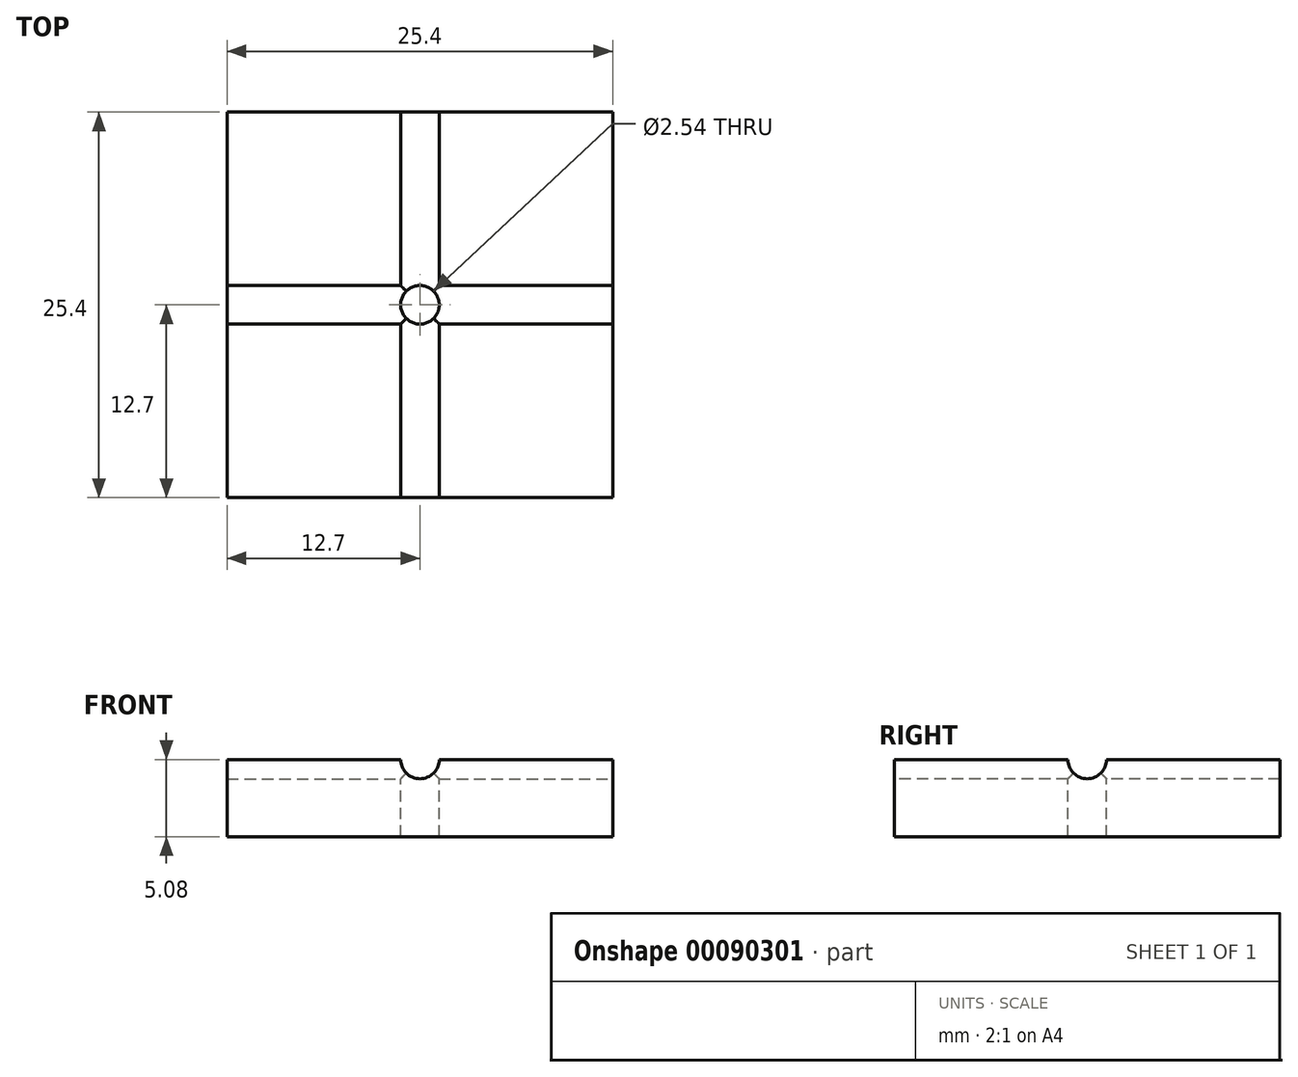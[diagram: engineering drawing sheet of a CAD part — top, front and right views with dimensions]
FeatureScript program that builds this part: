
annotation { "Feature Type Name" : "Feature", "Feature Type Description" : "" }
export const myFeature = defineFeature(function(context is Context, id is Id, definition is map)
    precondition{}
    {
        {
            var Q0;
            Q0=qCreatedBy(makeId("Top.planeOp"),FACE);
            var sketch = newSketch(context, id + "F0", { "sketchPlane" : qUnion([Q0])});
            skLineSegment(sketch, "E0.bottom", {"start": v(12.7, -12.7) * mm, "end": v(-12.7, -12.7) * mm});
            skLineSegment(sketch, "E0.top", {"start": v(12.7, 12.7) * mm, "end": v(-12.7, 12.7) * mm});
            skLineSegment(sketch, "E0.left", {"start": v(12.7, -12.7) * mm, "end": v(12.7, 12.7) * mm});
            skLineSegment(sketch, "E0.right", {"start": v(-12.7, -12.7) * mm, "end": v(-12.7, 12.7) * mm});
            skPoint(sketch, "E0.middle", {"position": v(0, 0) * mm});
            skSolve(sketch);
        }
        {
            var Q0;
            Q0=makeQuery(id+"F0.imprint","IMPRINT",FACE,{"disambiguationData":[TD([[makeQuery(id+"F0.imprint","IMPRINT",EDGE,{"derivedFrom":sQuery(id+"F0.wireOp",EDGE,"E0.bottom")}),-1.0]])]});
            extrude(context, id + "F1", {"entities" : qUnion([Q0]), "depth" : 5.08 * mm});
        }
        {
            var Q0;
            Q0=makeQuery(id+"F1.opExtrude","SWEPT_FACE",FACE,{"disambiguationData":[OSD([sQuery(id+"F0.wireOp",EDGE,"E0.left")])]});
            var sketch = newSketch(context, id + "F2", { "sketchPlane" : qUnion([Q0])});
            skCircle(sketch, "E1", {"center": v(0, 5.08) * mm, "radius": 1.27 * mm});
            skSolve(sketch);
        }
        {
            var Q0;
            {var subQ0=sQuery(id+"F2.wireOp",EDGE,"E1");var subQ1=makeQuery(id+"F1.opExtrude","CAP_EDGE",EDGE,{"disambiguationData":[OSD([sQuery(id+"F0.wireOp",EDGE,"E0.left")])],"isStart":false});var subQ2=makeQuery(id+"F2.imprint","INTERSECT",VERTEX,{"disambiguationData":[OD(0.0)],"derivedFrom":[subQ1,subQ0]});Q0=makeQuery(id+"F2.imprint","IMPRINT",FACE,{"disambiguationData":[TD([[makeQuery(id+"F2.imprint","IMPRINT",EDGE,{"disambiguationData":[TD([[subQ2,-1.0]])],"derivedFrom":subQ0}),1.0]])]});}
            extrude(context, id + "F3", {"entities" : qUnion([Q0]), "operationType" : NewBodyOperationType.REMOVE, "oppositeDirection" : true, "depth" : 25.4 * mm});
        }
        {
            var Q0;
            Q0=makeQuery(id+"F1.opExtrude","SWEPT_FACE",FACE,{"disambiguationData":[OSD([sQuery(id+"F0.wireOp",EDGE,"E0.bottom")])]});
            var sketch = newSketch(context, id + "F4", { "sketchPlane" : qUnion([Q0])});
            skCircle(sketch, "E2", {"center": v(0, 5.08) * mm, "radius": 1.27 * mm});
            skSolve(sketch);
        }
        {
            var Q0;
            {var subQ0=sQuery(id+"F4.wireOp",EDGE,"E2");var subQ1=makeQuery(id+"F1.opExtrude","CAP_EDGE",EDGE,{"disambiguationData":[OSD([sQuery(id+"F0.wireOp",EDGE,"E0.bottom")])],"isStart":false});var subQ2=makeQuery(id+"F4.imprint","INTERSECT",VERTEX,{"disambiguationData":[OD(0.0)],"derivedFrom":[subQ1,subQ0]});Q0=makeQuery(id+"F4.imprint","IMPRINT",FACE,{"disambiguationData":[TD([[makeQuery(id+"F4.imprint","IMPRINT",EDGE,{"disambiguationData":[TD([[subQ2,1.0]])],"derivedFrom":subQ0}),1.0]])]});}
            extrude(context, id + "F5", {"entities" : qUnion([Q0]), "operationType" : NewBodyOperationType.REMOVE, "oppositeDirection" : true, "depth" : 25.4 * mm});
        }
        {
            var Q0;
            {var subQ0=sQuery(id+"F0.wireOp",EDGE,"E0.bottom");var subQ1=makeQuery(id+"F1.opExtrude","SWEPT_FACE",FACE,{"disambiguationData":[OSD([subQ0])]});var subQ2=sQuery(id+"F0.wireOp",EDGE,"E0.left");var subQ3=makeQuery(id+"F1.opExtrude","SWEPT_FACE",FACE,{"disambiguationData":[OSD([subQ2])]});var subQ5=sQuery(id+"F0.wireOp",EDGE,"E0.right");Q0=makeQuery(id+"F5.boolean.opBoolean","SPLIT",FACE,{"disambiguationData":[TD([subQ3])],"derivedFrom":makeQuery(id+"F3.boolean.opBoolean","SPLIT",FACE,{"disambiguationData":[TD([subQ1])],"derivedFrom":makeQuery(id+"F1.opExtrude","CAP_FACE",FACE,{"disambiguationData":[OSD([subQ0,sQuery(id+"F0.wireOp",EDGE,"E0.top"),subQ2,subQ5])],"isStart":false})})});}
            var sketch = newSketch(context, id + "F6", { "sketchPlane" : qUnion([Q0])});
            skCircle(sketch, "E3", {"center": v(0, 0) * mm, "radius": 1.27 * mm});
            skSolve(sketch);
        }
        {
            var Q0;
            Q0=makeQuery(id+"F6.imprint","IMPRINT",FACE,{"disambiguationData":[TD([[makeQuery(id+"F6.imprint","IMPRINT",EDGE,{"derivedFrom":sQuery(id+"F6.wireOp",EDGE,"E3")}),1.0]])]});
            extrude(context, id + "F7", {"entities" : qUnion([Q0]), "operationType" : NewBodyOperationType.REMOVE, "oppositeDirection" : true, "depth" : 25.4 * mm});
        }
    });
